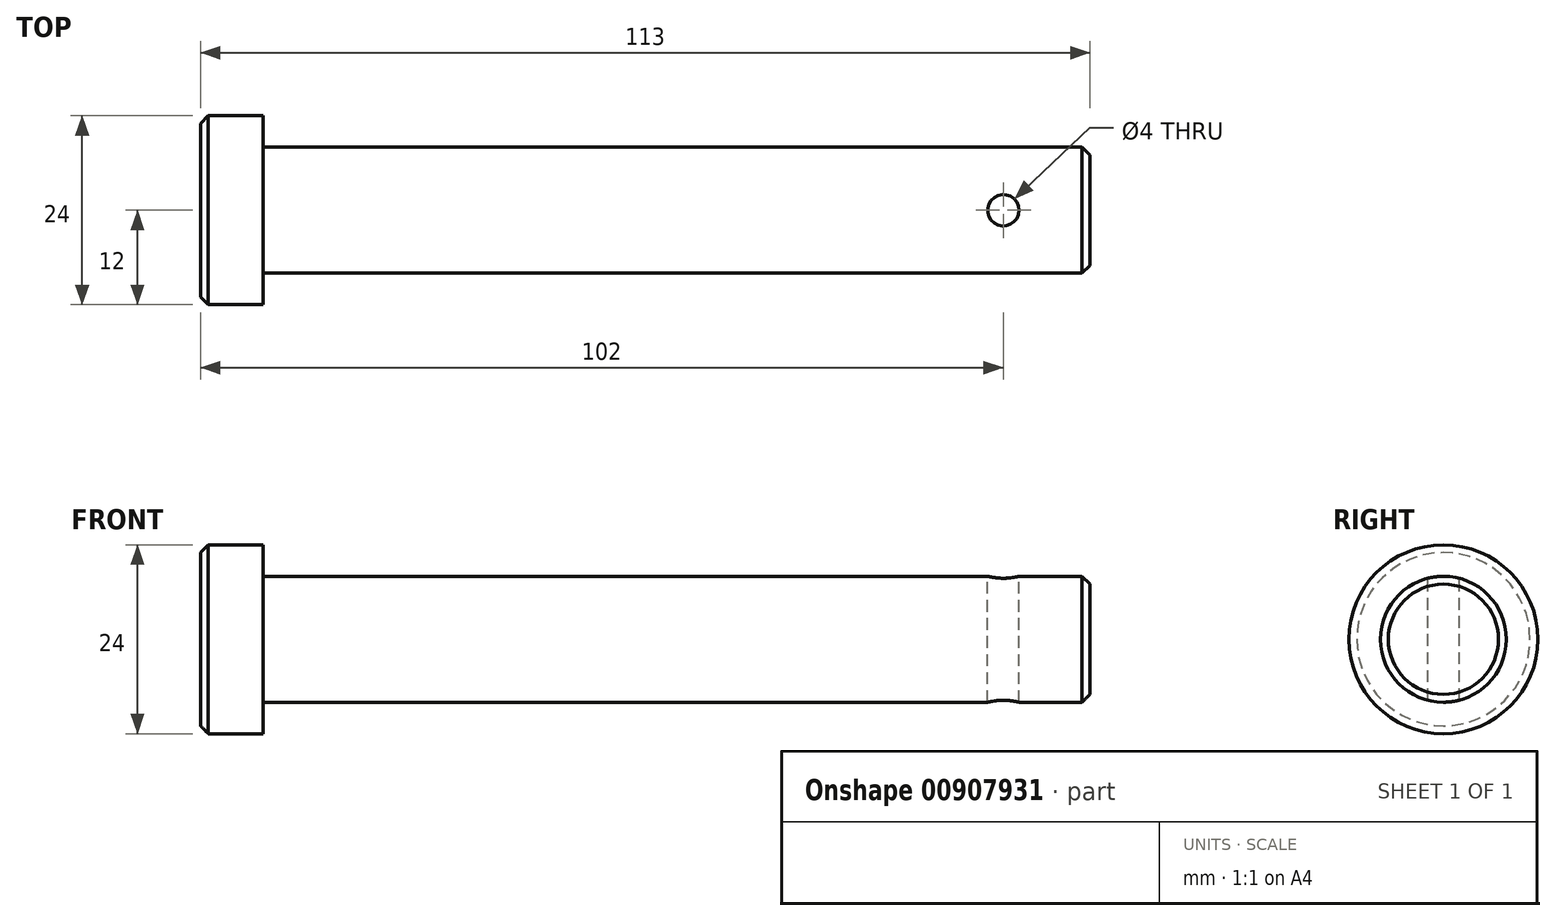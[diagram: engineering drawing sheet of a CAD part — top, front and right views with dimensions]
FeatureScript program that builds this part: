
annotation { "Feature Type Name" : "Feature", "Feature Type Description" : "" }
export const myFeature = defineFeature(function(context is Context, id is Id, definition is map)
    precondition{}
    {
        {
            var Q0;
            Q0=qCreatedBy(makeId("Right.planeOp"),FACE);
            var sketch = newSketch(context, id + "F0", { "sketchPlane" : qUnion([Q0])});
            skCircle(sketch, "E0", {"center": v(0, 0) * mm, "radius": 12 * mm});
            skSolve(sketch);
        }
        {
            var Q0;
            Q0 = qSketchRegion(id + "F0", true);
            extrude(context, id + "F1", {"entities" : qUnion([Q0]), "depth" : 8 * mm, "offsetDistance" : 25 * mm});
        }
        {
            var Q0;
            Q0=makeQuery(id+"F1.opExtrude","CAP_EDGE",EDGE,{"disambiguationData":[OSD([sQuery(id+"F0.wireOp",EDGE,"E0")])],"isStart":true});
            chamfer(context, id + "F2", {"entities" : qUnion([Q0]), "width" : 1 * mm, "tangentPropagation" : true});
        }
        {
            var Q0;
            Q0=makeQuery(id+"F1.opExtrude","CAP_FACE",FACE,{"disambiguationData":[OSD([sQuery(id+"F0.wireOp",EDGE,"E0")])],"isStart":false});
            var sketch = newSketch(context, id + "F3", { "sketchPlane" : qUnion([Q0])});
            skCircle(sketch, "E1", {"center": v(0, 0) * mm, "radius": 8 * mm});
            skSolve(sketch);
        }
        {
            var Q0;
            Q0 = qSketchRegion(id + "F3", true);
            extrude(context, id + "F4", {"entities" : qUnion([Q0]), "operationType" : NewBodyOperationType.ADD, "depth" : 105 * mm, "offsetDistance" : 25 * mm});
        }
        {
            var Q0;
            Q0=makeQuery(id+"F4.opExtrude","CAP_FACE",FACE,{"disambiguationData":[OSD([sQuery(id+"F3.wireOp",EDGE,"E1")])],"isStart":false});
            chamfer(context, id + "F5", {"entities" : qUnion([Q0]), "width" : 1 * mm, "tangentPropagation" : true});
        }
        {
            var Q0;
            Q0=qCreatedBy(makeId("Top.planeOp"),FACE);
            var sketch = newSketch(context, id + "F6", { "sketchPlane" : qUnion([Q0])});
            skLineSegment(sketch, "E2", {"start": v(0, 0) * mm, "end": v(57.72, 0) * mm, "construction": true});
            skCircle(sketch, "E3", {"center": v(102, 0) * mm, "radius": 2 * mm});
            skSolve(sketch);
        }
        {
            var Q0;
            Q0 = qSketchRegion(id + "F6", true);
            extrude(context, id + "F7", {"entities" : qUnion([Q0]), "operationType" : NewBodyOperationType.REMOVE, "endBound" : BoundingType.SYMMETRIC, "oppositeDirection" : true, "depth" : 60 * mm, "offsetDistance" : 25 * mm});
        }
    });
